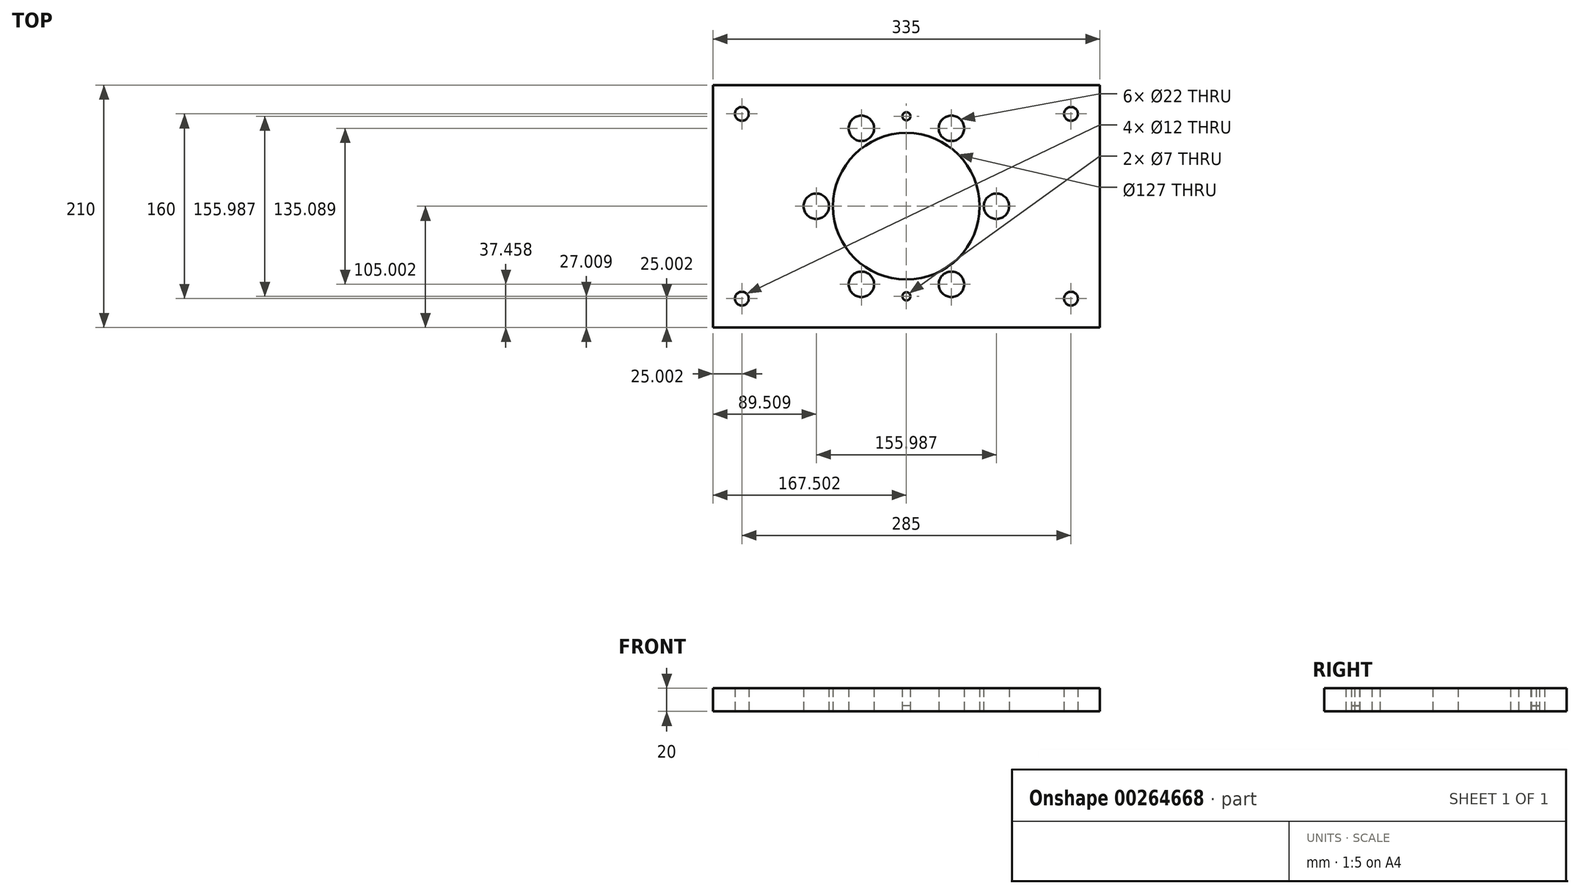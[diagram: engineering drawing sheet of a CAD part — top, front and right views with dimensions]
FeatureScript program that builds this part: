
annotation { "Feature Type Name" : "Feature", "Feature Type Description" : "" }
export const myFeature = defineFeature(function(context is Context, id is Id, definition is map)
    precondition{}
    {
        {
            var Q0;
            Q0=qCreatedBy(makeId("Top.planeOp"),FACE);
            var sketch = newSketch(context, id + "F0", { "sketchPlane" : qUnion([Q0])});
            skLineSegment(sketch, "E0.bottom", {"start": v(-278.67, -142.84) * mm, "end": v(56.33, -142.84) * mm});
            skLineSegment(sketch, "E0.top", {"start": v(-278.67, -352.84) * mm, "end": v(56.33, -352.84) * mm});
            skLineSegment(sketch, "E0.left", {"start": v(-278.67, -142.84) * mm, "end": v(-278.67, -352.84) * mm});
            skLineSegment(sketch, "E0.right", {"start": v(56.33, -142.84) * mm, "end": v(56.33, -352.84) * mm});
            skCircle(sketch, "E1", {"center": v(-253.67, -327.84) * mm, "radius": 6 * mm});
            skCircle(sketch, "E2", {"center": v(31.33, -327.84) * mm, "radius": 6 * mm});
            skCircle(sketch, "E3", {"center": v(31.33, -167.84) * mm, "radius": 6 * mm});
            skCircle(sketch, "E4", {"center": v(-253.67, -167.84) * mm, "radius": 6 * mm});
            skCircle(sketch, "E5", {"center": v(-111.17, -247.84) * mm, "radius": 63.5 * mm});
            skCircle(sketch, "E6.1.1", {"center": v(-111.17, -247.84) * mm, "radius": 78 * mm, "construction": true});
            skCircle(sketch, "E7", {"center": v(-111.17, -325.83) * mm, "radius": 3.5 * mm});
            skCircle(sketch, "E8", {"center": v(-189.16, -247.84) * mm, "radius": 11 * mm});
            skCircle(sketch, "E9.1.0", {"center": v(-150.16, -315.38) * mm, "radius": 11 * mm});
            skCircle(sketch, "E9.2.0", {"center": v(-72.17, -315.38) * mm, "radius": 11 * mm});
            skCircle(sketch, "E9.3.0", {"center": v(-33.17, -247.84) * mm, "radius": 11 * mm});
            skCircle(sketch, "E9.4.0", {"center": v(-72.17, -180.3) * mm, "radius": 11 * mm});
            skCircle(sketch, "E9.5.0", {"center": v(-150.16, -180.3) * mm, "radius": 11 * mm});
            skCircle(sketch, "E10.1.0", {"center": v(-111.17, -169.84) * mm, "radius": 3.5 * mm});
            skSolve(sketch);
        }
        {
            var Q0;
            Q0=makeQuery(id+"F0.imprint","IMPRINT",FACE,{"disambiguationData":[TD([[makeQuery(id+"F0.imprint","IMPRINT",EDGE,{"derivedFrom":sQuery(id+"F0.wireOp",EDGE,"E0.bottom")}),-1.0]])]});
            extrude(context, id + "F1", {"entities" : qUnion([Q0]), "depth" : 20 * mm});
        }
        {
            var Q0;
            Q0=makeQuery(id+"F0.imprint","IMPRINT",FACE,{"disambiguationData":[TD([[makeQuery(id+"F0.imprint","IMPRINT",EDGE,{"derivedFrom":sQuery(id+"F0.wireOp",EDGE,"E10.1.0")}),1.0]])]});
            var Q1;
            Q1=makeQuery(id+"F0.imprint","IMPRINT",FACE,{"disambiguationData":[TD([[makeQuery(id+"F0.imprint","IMPRINT",EDGE,{"derivedFrom":sQuery(id+"F0.wireOp",EDGE,"E7")}),1.0]])]});
            extrude(context, id + "F2", {"entities" : qUnion([Q0, Q1]), "depth" : 5 * mm});
        }
    });
